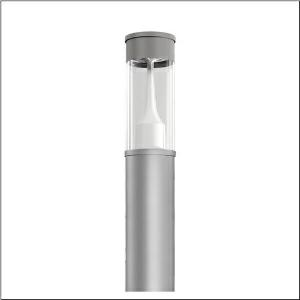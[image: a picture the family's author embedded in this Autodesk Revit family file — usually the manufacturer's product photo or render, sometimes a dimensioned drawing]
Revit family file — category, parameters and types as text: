
# Revit family: city-light_400_iq___st1_2a_5xa5305mf14hp_fa50
name_source: partatom
category: Lighting Fixtures
units: mm (PartAtom-declared; Revit-internal decimal feet)

## family parameters
Cut with Voids When Loaded = No
Host = Face
Light Source = No
Part Type = Normal
Room Calculation Point = No
Round Connector Dimension = Use Diameter
Shared = No

## types (1)
- --- (1 x LED, 4240 lm, 33.6 W, 2700K)
    Apparent Load = 34 VA
    CIE Flux Codes = 22 61 94 96 100
    Color Rendering = 70
    Color Temperature = 2700K
    Default Elevation = 1800 mm
    Description = City-Light 400 iQ, light pillar, Module 540 iQ-SR, primary light control with 3 zone facetted reflector, of plastic, silver coated, highly specular, structured, primary optical cover: cover, of PMMA, transparent, partly coated, light distribution: ST1.2a, primary light characteristic: asymmetric, LED, High Power LED, rated luminous flux: 4.240lm, luminous efficacy: 126lm/W, light colour: 727, colour temperature: 2700K, control gear: ECG iQ, control: pre-setting: logarithmic dimming characteristic, Street-Remote, Auto-Match, Temp-Guard, Lumen-Switch, Night-Set, Smart-Wire, Light-Fading, Desk-Remote (wireless, voltage-free reading and setting of iQ features in the workshop via application-optimized NFC function/RFID function), optimised constant luminous flux control (CLO 2.0), with terminal, 6-pole, max. 2.5mm², mains connection: 230..240V, AC, 50/60Hz, start of lifetime: 34W, end of service life: 36W, reduction: 15W, luminaire housing, cylindrical, of extruded aluminium section, coated, Siteco® metallic grey (DB 702S), length: 4.694mm, diameter: 200mm, Module 540 iQ-SR, traffic white (RAL 9016), equipment: Power, protection rating (complete): IP65, insulation class (complete): insulation class II (safety insulation), certification: CE, ENEC, VDE, packaging unit: 1 piece

Light Distribution: ST1.2a
    Height = 500 mm
    Lamp = 1 x LED
    Lamp Light Flux = 4240 lm
    Lamp Power = 33.6 W
    Lamp count = 1
    Length = 200 mm  [stored 0.656168 ft]
    Luminous efficacy = 126 lm/W
    Manufacturer = Siteco
    ModVariant = No
    Model = 5XA5305MF14HP
    Mounting Place = Floor
    Mounting Type = Freestanding
    Number of Poles = 1
    OnlyDefault = Yes
    Power Factor = 1
    Product Name = City-Light 400 iQ | ST1.2a
    Product group = light pillar
    ProductGroupID = 1301
    Protection Class = Protection class II
    Protection Degree = IP 65
    RLX_Detail_Level = 1
    RLX_Emergency_Light_Flux = 0 lm
    RLX_Emergency_Type = 0
    RLX_Emergency_Type_DB = No
    RlxData = <blob elided: 53425 chars, md5=0a038e4f>
    Socket = socket
    Standby Power = 0 W
    System Light Flux = 4240 lm
    System Power = 34 W
    Type Comments = factory setting: luminous flux: 100 % | dim-lin: 254 | 695 mA
    Type Image = l_1006916.jpg
    URL = http://relux.com
    VarID = @adj_122875
    Voltage = 0 V
    Weight = 0.00 kg
    Width = 0 mm  [stored 0 ft]

note: [stored X ft] marks values corroborated as IEEE doubles in the binary element streams (Revit-internal decimal feet)

## geometry (parser evidence)
native form markers: Blend x4, Sweep x10
no freeform markers — native parametric forms only
